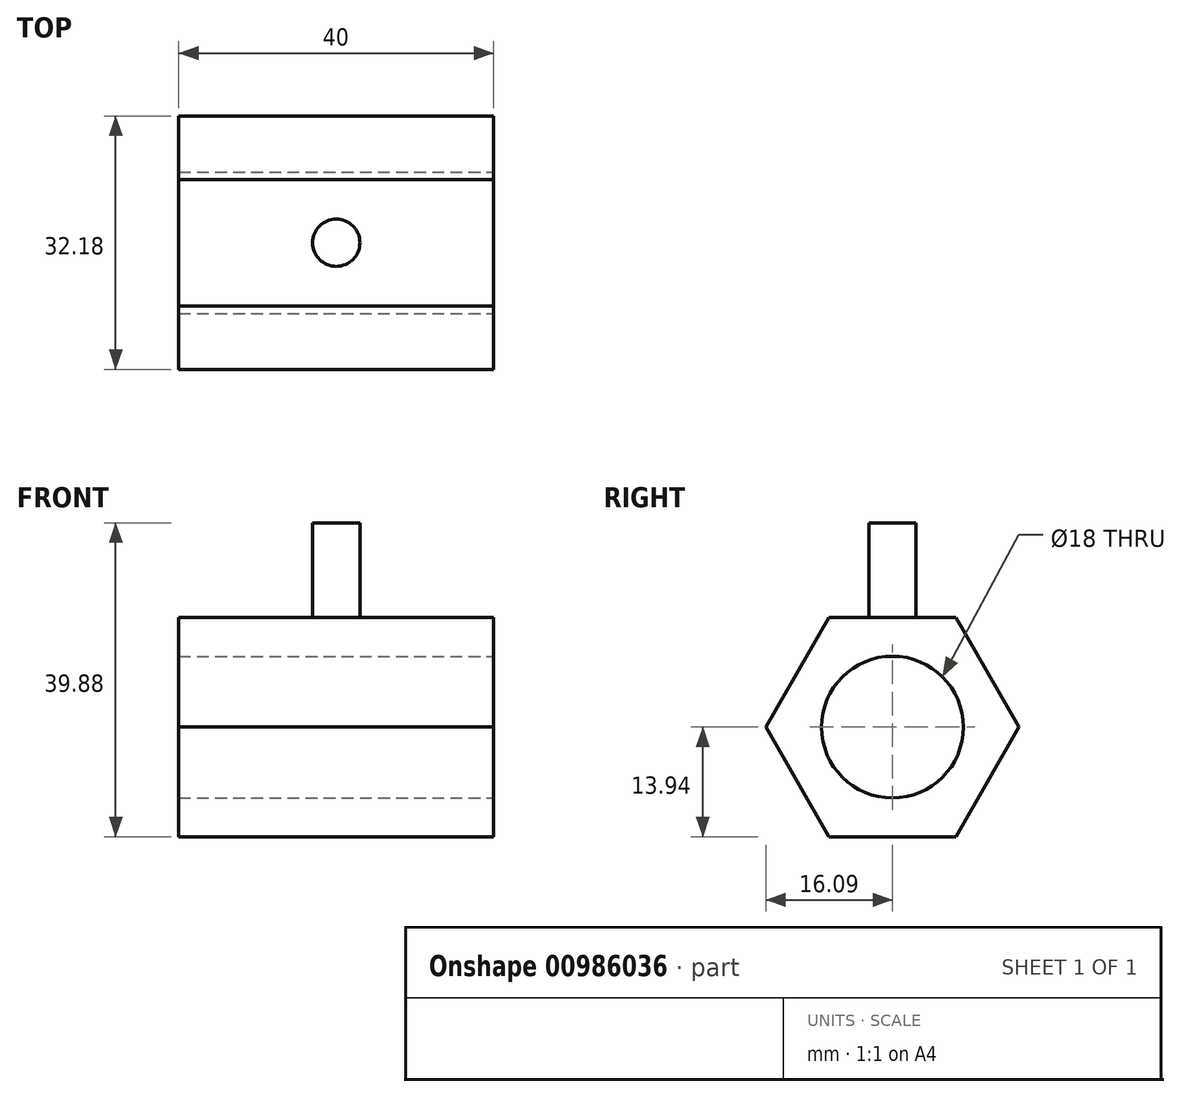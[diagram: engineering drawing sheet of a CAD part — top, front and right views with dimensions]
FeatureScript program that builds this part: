
annotation { "Feature Type Name" : "Feature", "Feature Type Description" : "" }
export const myFeature = defineFeature(function(context is Context, id is Id, definition is map)
    precondition{}
    {
        {
            var Q0;
            Q0=qCreatedBy(makeId("Right.planeOp"),FACE);
            var sketch = newSketch(context, id + "F0", { "sketchPlane" : qUnion([Q0])});
            skLineSegment(sketch, "E0", {"start": v(-8.05, 13.94) * mm, "end": v(8.05, 13.94) * mm});
            skLineSegment(sketch, "E1", {"start": v(8.05, 13.94) * mm, "end": v(16.1, 0) * mm});
            skLineSegment(sketch, "E2", {"start": v(8.05, -13.94) * mm, "end": v(16.1, 0) * mm});
            skLineSegment(sketch, "E3", {"start": v(8.05, -13.94) * mm, "end": v(-8.05, -13.94) * mm});
            skLineSegment(sketch, "E4", {"start": v(-16.1, 0) * mm, "end": v(-8.05, -13.94) * mm});
            skLineSegment(sketch, "E5", {"start": v(-16.1, 0) * mm, "end": v(-8.05, 13.94) * mm});
            skPoint(sketch, "E6.MirrorCS.start.orphan", {"position": v(0, 0) * mm});
            skCircle(sketch, "E7", {"center": v(0, 0) * mm, "radius": 9 * mm});
            skSolve(sketch);
        }
        {
            var Q0;
            Q0=makeQuery(id+"F0.imprint","IMPRINT",FACE,{"disambiguationData":[TD([[makeQuery(id+"F0.imprint","IMPRINT",EDGE,{"derivedFrom":sQuery(id+"F0.wireOp",EDGE,"E0")}),-1.0]])]});
            extrude(context, id + "F1", {"entities" : qUnion([Q0]), "oppositeDirection" : true, "depth" : 40 * mm, "offsetDistance" : 25 * mm});
        }
        {
            var Q0;
            Q0=makeQuery(id+"F1.opExtrude","SWEPT_FACE",FACE,{"disambiguationData":[OSD([sQuery(id+"F0.wireOp",EDGE,"E0")])]});
            cPlane(context, id + "F2", {"entities" : qUnion([Q0]), "cplaneType" : CPlaneType.OFFSET, "offset" : 0 * mm, "width" : 150 * mm, "height" : 150 * mm});
        }
        {
            var Q0;
            Q0=qCreatedBy(id+"F2.planeOp",FACE);
            var sketch = newSketch(context, id + "F3", { "sketchPlane" : qUnion([Q0])});
            skLineSegment(sketch, "E8", {"start": v(0, 0) * mm, "end": v(-20, 0) * mm});
            skCircle(sketch, "E9", {"center": v(-20, 0) * mm, "radius": 3 * mm});
            skSolve(sketch);
        }
        {
            var Q0;
            Q0=makeQuery(id+"F3.imprint","IMPRINT",FACE,{"disambiguationData":[TD([[makeQuery(id+"F3.imprint","IMPRINT",EDGE,{"derivedFrom":sQuery(id+"F3.wireOp",EDGE,"E9")}),1.0]])]});
            extrude(context, id + "F4", {"entities" : qUnion([Q0]), "operationType" : NewBodyOperationType.ADD, "depth" : 12 * mm, "offsetDistance" : 25 * mm});
        }
    });
